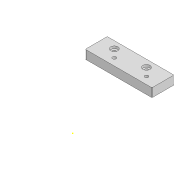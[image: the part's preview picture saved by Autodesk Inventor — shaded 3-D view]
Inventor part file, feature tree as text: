
AUTODESK INVENTOR PART (.ipt)
format: ipt  version: 2020 (Build 240168000, 168)  size: 250,368 bytes
history: native  units: mm
features: sketch x9, extrude x8, other x4, fillet x2
ambient origin geometry x8: Origin, YZ Plane, XZ Plane, XY Plane, X Axis, Y Axis, Z Axis, Center Point
bodies: Body1 (feature_tree)
feature tree (23):
  other  "Sólido1"
  extrude  "Extrusão1"  Depth=140.0mm
  extrude  "Extrusão2"  Depth=4.3mm
  sketch  "Esboço3"  dims[d4=4.3mm d5=4.3mm]
  extrude  "Extrusão3"  Depth=4.3mm
  extrude  "Extrusão4"  Depth=10.0mm
  extrude  "Extrusão5"  Depth=20.0mm
  extrude  "Extrusão6"  Depth=20.0mm
  extrude  "Extrusão7"  Depth=11.0mm
  fillet  "Arredondamento1"  Radius=11.0mm
  extrude  "Extrusão8"  Depth=9.0mm
  fillet  "Arredondamento2"  Radius=9.0mm
  sketch  "Esboço1"  dims[d0=77.0mm d1=140.0mm]
  sketch  "Esboço2"  dims[d2=4.3mm d3=4.3mm]
  sketch  "Esboço4"  dims[d6=10.0mm d7=10.0mm]
  sketch  "Esboço5"  dims[d8=20.0mm d9=20.0mm]
  sketch  "Esboço6"  dims[d10=20.0mm d11=20.0mm]
  other  "Contorno projetado1"
  sketch  "Esboço7"  dims[d12=26.0mm d13=26.0mm d14=11.0mm d15=0.0mm]
  other  "Contorno projetado2"
  sketch  "Esboço8"  dims[d16=9.0mm d17=9.0mm d18=9.0mm]
  other  "Contorno projetado3"
  sketch  "Esboço9"  dims[d19=9.0mm d20=3.0mm d21=0.0mm d22=4.4mm d23=4.4mm d24=10.0mm d25=10.0mm d26=10.0mm d27=10.0mm d28=4.4mm d29=4.4mm d30=10.0mm d31=10.0mm d32=10.0mm d33=10.0mm d34=12.0mm d35=0.0mm d36=6.95mm d37=6.95mm d38=6.95mm d39=6.95mm d40=6.5mm d41=0.0mm d42=0.5mm d43=0.0mm d44=0.5mm d45=0.0mm d46=8.0mm d47=0.0mm d48=1.0mm d49=9.0mm d50=9.0mm d51=22.0mm d52=0.0mm d53=1.0mm]
